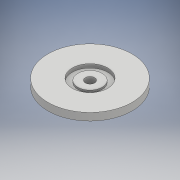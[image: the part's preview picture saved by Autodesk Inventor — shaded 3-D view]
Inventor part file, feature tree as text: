
AUTODESK INVENTOR PART (.ipt)
format: ipt  version: 2017 (Build 210142000, 142)  size: 180,736 bytes
history: native  units: mm
features: sketch x6, extrude x5, revolve x1
ambient origin geometry x8: Origin, YZ Plane, XZ Plane, XY Plane, X Axis, Y Axis, Z Axis, Center Point
bodies: Body1 (feature_tree)
feature tree (12):
  revolve  "Revolution2"  [1 undecoded]
  extrude  "Extrusion6"  Depth=7.0mm
  extrude  "Extrusion7"  Depth=4.0mm
  extrude  "Extrusion8"  Depth=4.0mm
  extrude  "Extrusion9"  Depth=4.0mm
  extrude  "Extrusion10"  Depth=4.0mm
  sketch  "Sketch1"  dims[d1=2.5mm d2=4.0mm]
  sketch  "Sketch6"  dims[d3=7.0mm d4=20.0mm]
  sketch  "Sketch7"  dims[d5=34.0mm d9=4.0mm]
  sketch  "Sketch8"  dims[d12=2.5mm d13=4.0mm]
  sketch  "Sketch9"  dims[d55=22.5mm d56=4.0mm]
  sketch  "Sketch10"  dims[d57=90.0deg d64=20.0mm d65=90.0deg d69=15.0mm d71=15.0mm d73=5.0mm d74=0.0mm d75=2.5mm d76=5.0mm d77=5.0mm d78=26.0mm d79=0.0mm d80=3.0mm d81=3.0mm d82=3.0mm d83=3.0mm d84=4.0mm d85=0.0mm d86=100.0mm d87=0.0mm d88=5.0mm d89=0.0mm]
note: 1 required parameter value undecoded (feature->parameter linkage not recoverable at this tier; creation-order binding heuristic only, values carry confidence <= 0.55)
